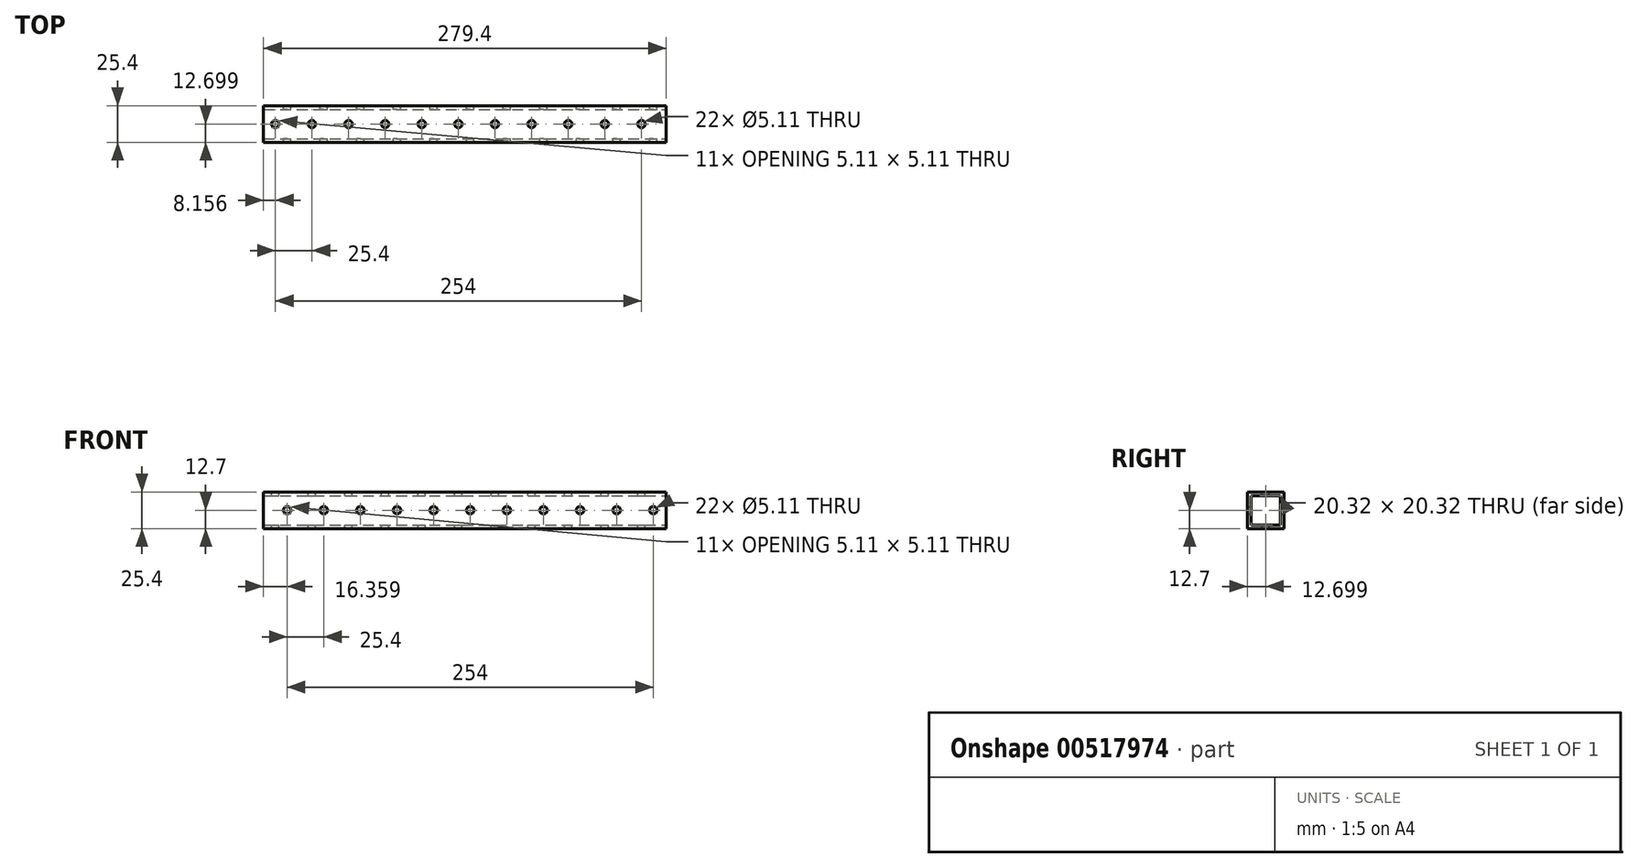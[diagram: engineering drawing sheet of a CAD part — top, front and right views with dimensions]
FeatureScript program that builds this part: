
annotation { "Feature Type Name" : "Feature", "Feature Type Description" : "" }
export const myFeature = defineFeature(function(context is Context, id is Id, definition is map)
    precondition{}
    {
        {
            var Q0;
            Q0=qCreatedBy(makeId("Top.planeOp"),FACE);
            var sketch = newSketch(context, id + "F0", { "sketchPlane" : qUnion([Q0])});
            skLineSegment(sketch, "E0.bottom", {"start": v(-151.62, 0.36) * mm, "end": v(127.78, 0.36) * mm});
            skLineSegment(sketch, "E0.top", {"start": v(-151.62, -25.04) * mm, "end": v(127.78, -25.04) * mm});
            skLineSegment(sketch, "E0.left", {"start": v(-151.62, 0.36) * mm, "end": v(-151.62, -25.04) * mm});
            skLineSegment(sketch, "E0.right", {"start": v(127.78, 0.36) * mm, "end": v(127.78, -25.04) * mm});
            skSolve(sketch);
        }
        {
            var Q0;
            Q0=makeQuery(id+"F0.imprint","IMPRINT",FACE,{"disambiguationData":[TD([[makeQuery(id+"F0.imprint","IMPRINT",EDGE,{"derivedFrom":sQuery(id+"F0.wireOp",EDGE,"E0.bottom")}),-1.0]])]});
            extrude(context, id + "F1", {"entities" : qUnion([Q0]), "depth" : 25.4 * mm, "offsetDistance" : 25.4 * mm});
        }
        {
            var Q0;
            Q0=makeQuery(id+"F1.opExtrude","SWEPT_FACE",FACE,{"disambiguationData":[OSD([sQuery(id+"F0.wireOp",EDGE,"E0.right")])]});
            var sketch = newSketch(context, id + "F2", { "sketchPlane" : qUnion([Q0])});
            skLineSegment(sketch, "E1.bottom", {"start": v(-22.5, 22.86) * mm, "end": v(-2.18, 22.86) * mm});
            skLineSegment(sketch, "E1.top", {"start": v(-22.5, 2.54) * mm, "end": v(-2.18, 2.54) * mm});
            skLineSegment(sketch, "E1.left", {"start": v(-22.5, 22.86) * mm, "end": v(-22.5, 2.54) * mm});
            skLineSegment(sketch, "E1.right", {"start": v(-2.18, 22.86) * mm, "end": v(-2.18, 2.54) * mm});
            skSolve(sketch);
        }
        {
            var Q0;
            Q0=makeQuery(id+"F2.imprint","IMPRINT",FACE,{"disambiguationData":[TD([[makeQuery(id+"F2.imprint","IMPRINT",EDGE,{"derivedFrom":sQuery(id+"F2.wireOp",EDGE,"E1.bottom")}),-1.0]])]});
            extrude(context, id + "F3", {"entities" : qUnion([Q0]), "operationType" : NewBodyOperationType.REMOVE, "oppositeDirection" : true, "depth" : 279.4 * mm, "offsetDistance" : 25.4 * mm});
        }
        {
            var Q0;
            Q0=makeQuery(id+"F1.opExtrude","CAP_FACE",FACE,{"disambiguationData":[OSD([sQuery(id+"F0.wireOp",EDGE,"E0.bottom"),sQuery(id+"F0.wireOp",EDGE,"E0.top"),sQuery(id+"F0.wireOp",EDGE,"E0.left"),sQuery(id+"F0.wireOp",EDGE,"E0.right")])],"isStart":false});
            var sketch = newSketch(context, id + "F4", { "sketchPlane" : qUnion([Q0])});
            skCircle(sketch, "E2", {"center": v(-143.46, -12.34) * mm, "radius": 2.55 * mm});
            skCircle(sketch, "E3.1.0.0", {"center": v(-118.06, -12.34) * mm, "radius": 2.55 * mm});
            skCircle(sketch, "E3.2.0.0", {"center": v(-92.66, -12.34) * mm, "radius": 2.55 * mm});
            skCircle(sketch, "E3.3.0.0", {"center": v(-67.26, -12.34) * mm, "radius": 2.55 * mm});
            skCircle(sketch, "E3.4.0.0", {"center": v(-41.86, -12.34) * mm, "radius": 2.55 * mm});
            skCircle(sketch, "E3.5.0.0", {"center": v(-16.46, -12.34) * mm, "radius": 2.55 * mm});
            skCircle(sketch, "E3.6.0.0", {"center": v(8.94, -12.34) * mm, "radius": 2.55 * mm});
            skCircle(sketch, "E3.7.0.0", {"center": v(34.34, -12.34) * mm, "radius": 2.55 * mm});
            skCircle(sketch, "E3.8.0.0", {"center": v(59.74, -12.34) * mm, "radius": 2.55 * mm});
            skCircle(sketch, "E3.9.0.0", {"center": v(85.14, -12.34) * mm, "radius": 2.55 * mm});
            skCircle(sketch, "E3.10.0.0", {"center": v(110.54, -12.34) * mm, "radius": 2.55 * mm});
            skLineSegment(sketch, "E3.direction1", {"start": v(-143.46, -12.34) * mm, "end": v(-118.06, -12.34) * mm, "construction": true});
            skSolve(sketch);
        }
        {
            var Q0;
            Q0=makeQuery(id+"F1.opExtrude","SWEPT_FACE",FACE,{"disambiguationData":[OSD([sQuery(id+"F0.wireOp",EDGE,"E0.bottom")])]});
            var sketch = newSketch(context, id + "F5", { "sketchPlane" : qUnion([Q0])});
            skCircle(sketch, "E4", {"center": v(-118.74, 12.7) * mm, "radius": 2.55 * mm});
            skCircle(sketch, "E5.1.0.0", {"center": v(-93.34, 12.7) * mm, "radius": 2.55 * mm});
            skCircle(sketch, "E5.2.0.0", {"center": v(-67.94, 12.7) * mm, "radius": 2.55 * mm});
            skCircle(sketch, "E5.3.0.0", {"center": v(-42.54, 12.7) * mm, "radius": 2.55 * mm});
            skCircle(sketch, "E5.4.0.0", {"center": v(-17.14, 12.7) * mm, "radius": 2.55 * mm});
            skCircle(sketch, "E5.5.0.0", {"center": v(8.26, 12.7) * mm, "radius": 2.55 * mm});
            skCircle(sketch, "E5.6.0.0", {"center": v(33.66, 12.7) * mm, "radius": 2.55 * mm});
            skCircle(sketch, "E5.7.0.0", {"center": v(59.06, 12.7) * mm, "radius": 2.55 * mm});
            skCircle(sketch, "E5.8.0.0", {"center": v(84.46, 12.7) * mm, "radius": 2.55 * mm});
            skCircle(sketch, "E5.9.0.0", {"center": v(109.86, 12.7) * mm, "radius": 2.55 * mm});
            skCircle(sketch, "E5.10.0.0", {"center": v(135.26, 12.7) * mm, "radius": 2.55 * mm});
            skLineSegment(sketch, "E5.direction1", {"start": v(-118.74, 12.7) * mm, "end": v(-93.34, 12.7) * mm, "construction": true});
            skSolve(sketch);
        }
        {
            var Q0;
            Q0=sQuery(id+"F5.wireOp",VERTEX,"E5.5.0.0.center");
            var Q1;
            Q1=sQuery(id+"F5.wireOp",VERTEX,"E5.10.0.0.center");
            var Q2;
            Q2=sQuery(id+"F5.wireOp",VERTEX,"E5.1.0.0.center");
            var Q3;
            Q3=sQuery(id+"F5.wireOp",VERTEX,"E5.9.0.0.center");
            var Q4;
            Q4=sQuery(id+"F5.wireOp",VERTEX,"E5.4.0.0.center");
            var Q5;
            Q5=sQuery(id+"F5.wireOp",VERTEX,"E5.2.0.0.center");
            var Q6;
            Q6=sQuery(id+"F5.wireOp",VERTEX,"E5.6.0.0.center");
            var Q7;
            Q7=sQuery(id+"F5.wireOp",VERTEX,"E4.center");
            var Q8;
            Q8=sQuery(id+"F5.wireOp",VERTEX,"E5.3.0.0.center");
            var Q9;
            Q9=sQuery(id+"F5.wireOp",VERTEX,"E5.7.0.0.center");
            var Q10;
            Q10=sQuery(id+"F5.wireOp",VERTEX,"E5.8.0.0.center");
            var Q11;
            Q11=makeQuery(id+"F1.opExtrude","SWEPT_BODY",BODY,{"disambiguationData":[OSD([sQuery(id+"F0.wireOp",EDGE,"E0.bottom"),sQuery(id+"F0.wireOp",EDGE,"E0.top"),sQuery(id+"F0.wireOp",EDGE,"E0.left"),sQuery(id+"F0.wireOp",EDGE,"E0.right")])]});
            hole(context, id + "F6", {"style" : HoleStyle.SIMPLE, "endStyle" : HoleEndStyle.THROUGH, "holeDiameter" : 5.1 * mm, "isTappedThrough" : true, "tappedDepth" : 12.7 * mm, "tapClearance" : 3, "locations" : qUnion([Q0, Q1, Q2, Q3, Q4, Q5, Q6, Q7, Q8, Q9, Q10]), "scope" : qUnion([Q11])});
        }
        {
            var Q0;
            Q0=sQuery(id+"F4.wireOp",VERTEX,"E3.7.0.0.center");
            var Q1;
            Q1=sQuery(id+"F4.wireOp",VERTEX,"E3.2.0.0.center");
            var Q2;
            Q2=sQuery(id+"F4.wireOp",VERTEX,"E3.5.0.0.center");
            var Q3;
            Q3=sQuery(id+"F4.wireOp",VERTEX,"E3.4.0.0.center");
            var Q4;
            Q4=sQuery(id+"F4.wireOp",VERTEX,"E3.6.0.0.center");
            var Q5;
            Q5=sQuery(id+"F4.wireOp",VERTEX,"E3.8.0.0.center");
            var Q6;
            Q6=sQuery(id+"F4.wireOp",VERTEX,"E3.3.0.0.center");
            var Q7;
            Q7=sQuery(id+"F4.wireOp",VERTEX,"E3.direction1.start");
            var Q8;
            Q8=sQuery(id+"F4.wireOp",VERTEX,"E3.1.0.0.center");
            var Q9;
            Q9=sQuery(id+"F4.wireOp",VERTEX,"E3.9.0.0.center");
            var Q10;
            Q10=sQuery(id+"F4.wireOp",VERTEX,"E3.10.0.0.center");
            var Q11;
            Q11=makeQuery(id+"F1.opExtrude","SWEPT_BODY",BODY,{"disambiguationData":[OSD([sQuery(id+"F0.wireOp",EDGE,"E0.bottom"),sQuery(id+"F0.wireOp",EDGE,"E0.top"),sQuery(id+"F0.wireOp",EDGE,"E0.left"),sQuery(id+"F0.wireOp",EDGE,"E0.right")])]});
            hole(context, id + "F7", {"style" : HoleStyle.SIMPLE, "endStyle" : HoleEndStyle.THROUGH, "holeDiameter" : 5.1 * mm, "isTappedThrough" : true, "tappedDepth" : 12.7 * mm, "tapClearance" : 3, "locations" : qUnion([Q0, Q1, Q2, Q3, Q4, Q5, Q6, Q7, Q8, Q9, Q10]), "scope" : qUnion([Q11])});
        }
    });
